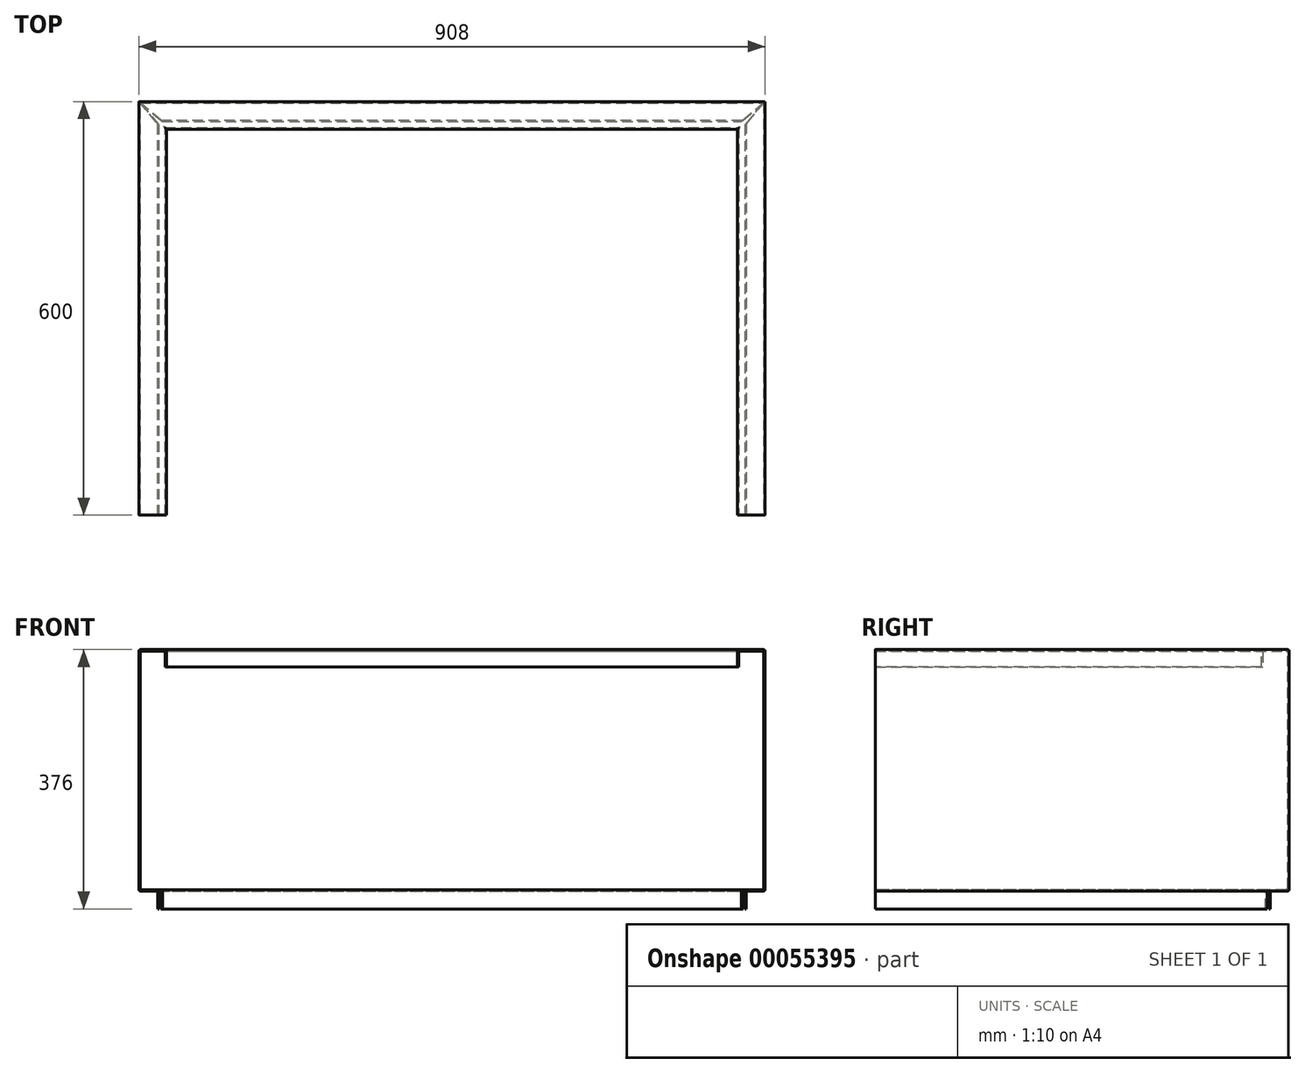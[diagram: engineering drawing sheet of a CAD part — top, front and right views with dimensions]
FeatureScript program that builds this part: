
annotation { "Feature Type Name" : "Feature", "Feature Type Description" : "" }
export const myFeature = defineFeature(function(context is Context, id is Id, definition is map)
    precondition{}
    {
        {
            var Q0;
            Q0=qCreatedBy(makeId("Front.planeOp"),FACE);
            var sketch = newSketch(context, id + "F0", { "sketchPlane" : qUnion([Q0])});
            skLineSegment(sketch, "E0", {"start": v(40, -25) * mm, "end": v(40, 0) * mm});
            skLineSegment(sketch, "E1", {"start": v(40, 0) * mm, "end": v(0, 0) * mm});
            skLineSegment(sketch, "E2", {"start": v(0, 0) * mm, "end": v(0, -350) * mm});
            skLineSegment(sketch, "E3", {"start": v(0, -350) * mm, "end": v(27, -350) * mm});
            skLineSegment(sketch, "E4", {"start": v(27, -350) * mm, "end": v(27, -376) * mm});
            skLineSegment(sketch, "E5.0", {"start": v(29, -348) * mm, "end": v(29, -376) * mm});
            skLineSegment(sketch, "E5.1", {"start": v(38, -25) * mm, "end": v(38, -2) * mm});
            skLineSegment(sketch, "E5.2", {"start": v(38, -2) * mm, "end": v(2, -2) * mm});
            skLineSegment(sketch, "E5.3", {"start": v(2, -2) * mm, "end": v(2, -348) * mm});
            skLineSegment(sketch, "E5.4", {"start": v(2, -348) * mm, "end": v(29, -348) * mm});
            skLineSegment(sketch, "E6", {"start": v(38, -25) * mm, "end": v(40, -25) * mm});
            skLineSegment(sketch, "E7", {"start": v(27, -376) * mm, "end": v(29, -376) * mm});
            skSolve(sketch);
        }
        {
            var Q0;
            Q0=qCreatedBy(makeId("Top.planeOp"),FACE);
            var sketch = newSketch(context, id + "F1", { "sketchPlane" : qUnion([Q0])});
            skLineSegment(sketch, "E8", {"start": v(0, 0) * mm, "end": v(0, 600) * mm});
            skLineSegment(sketch, "E9", {"start": v(0, 600) * mm, "end": v(908, 600) * mm});
            skLineSegment(sketch, "E10", {"start": v(908, 600) * mm, "end": v(908, 0) * mm});
            skSolve(sketch);
        }
        {
            var Q0;
            Q0=qSketchRegion(id+"F0",true);
            var Q1;
            Q1=qConstructionFilter(qBodyType(qCreatedBy(id+"F1",EDGE),BodyType.WIRE),ConstructionObject.NO);
            sweep(context, id + "F2", {"profiles" : qUnion([Q0]), "path" : qUnion([Q1])});
        }
        {
            var Q0;
            Q0=makeQuery(id+"F2.opSweep","SWEPT_FACE",FACE,{"disambiguationData":[OSD([sQuery(id+"F0.wireOp",EDGE,"E5.4"),sQuery(id+"F1.wireOp",EDGE,"E8")])]});
            var sketch = newSketch(context, id + "F3", { "sketchPlane" : qUnion([Q0])});
            skLineSegment(sketch, "E11", {"start": v(2, 598) * mm, "end": v(29, 565.82) * mm});
            skLineSegment(sketch, "E12", {"start": v(29, 565.82) * mm, "end": v(34.18, 571) * mm});
            skLineSegment(sketch, "E13", {"start": v(34.18, 571) * mm, "end": v(2, 598) * mm});
            skLineSegment(sketch, "E14", {"start": v(906, 598) * mm, "end": v(879, 565.82) * mm});
            skLineSegment(sketch, "E15", {"start": v(879, 565.82) * mm, "end": v(873.82, 571) * mm});
            skLineSegment(sketch, "E16", {"start": v(873.82, 571) * mm, "end": v(906, 598) * mm});
            skSolve(sketch);
        }
        {
            var Q0;
            {var subQ0=sQuery(id+"F3.wireOp",EDGE,"E14");Q0=makeQuery(id+"F3.imprint","IMPRINT",FACE,{"disambiguationData":[TD([[makeQuery(id+"F3.imprint","IMPRINT",EDGE,{"derivedFrom":subQ0}),-1.0]])]});}
            var Q1;
            {var subQ0=sQuery(id+"F3.wireOp",EDGE,"E11");Q1=makeQuery(id+"F3.imprint","IMPRINT",FACE,{"disambiguationData":[TD([[makeQuery(id+"F3.imprint","IMPRINT",EDGE,{"derivedFrom":subQ0}),1.0]])]});}
            extrude(context, id + "F4", {"entities" : qUnion([Q0, Q1]), "operationType" : NewBodyOperationType.REMOVE, "oppositeDirection" : true, "depth" : 30 * mm});
        }
        {
            var Q0;
            Q0=makeQuery(id+"F2.opSweep","SWEPT_EDGE",EDGE,{"disambiguationData":[OSD([sQuery(id+"F0.wireOp",EDGE,"E0"),sQuery(id+"F0.wireOp",EDGE,"E1"),sQuery(id+"F1.wireOp",EDGE,"E8")])]});
            var Q1;
            Q1=makeQuery(id+"F2.opSweep","SWEPT_EDGE",EDGE,{"disambiguationData":[OSD([sQuery(id+"F0.wireOp",EDGE,"E1"),sQuery(id+"F0.wireOp",EDGE,"E2"),sQuery(id+"F1.wireOp",EDGE,"E8")])]});
            var Q2;
            Q2=makeQuery(id+"F2.opSweep","SWEPT_EDGE",EDGE,{"disambiguationData":[OSD([sQuery(id+"F0.wireOp",EDGE,"E0"),sQuery(id+"F0.wireOp",EDGE,"E1"),sQuery(id+"F1.wireOp",EDGE,"E9")])]});
            var Q3;
            Q3=makeQuery(id+"F2.opSweep","SWEPT_EDGE",EDGE,{"disambiguationData":[OSD([sQuery(id+"F0.wireOp",EDGE,"E1"),sQuery(id+"F0.wireOp",EDGE,"E2"),sQuery(id+"F1.wireOp",EDGE,"E9")])]});
            var Q4;
            Q4=makeQuery(id+"F2.opSweep","SWEPT_EDGE",EDGE,{"disambiguationData":[OSD([sQuery(id+"F0.wireOp",EDGE,"E0"),sQuery(id+"F0.wireOp",EDGE,"E1"),sQuery(id+"F1.wireOp",EDGE,"E10")])]});
            var Q5;
            Q5=makeQuery(id+"F2.opSweep","SWEPT_EDGE",EDGE,{"disambiguationData":[OSD([sQuery(id+"F0.wireOp",EDGE,"E1"),sQuery(id+"F0.wireOp",EDGE,"E2"),sQuery(id+"F1.wireOp",EDGE,"E10")])]});
            var Q6;
            Q6=makeQuery(id+"F2.opSweep","MID_CAP_EDGE",EDGE,{"disambiguationData":[OSD([sQuery(id+"F0.wireOp",EDGE,"E2"),sQuery(id+"F1.wireOp",VERTEX,"E10.start")])],"capPos":2.0});
            var Q7;
            Q7=makeQuery(id+"F2.opSweep","SWEPT_EDGE",EDGE,{"disambiguationData":[OSD([sQuery(id+"F0.wireOp",EDGE,"E2"),sQuery(id+"F0.wireOp",EDGE,"E3"),sQuery(id+"F1.wireOp",EDGE,"E10")])]});
            var Q8;
            Q8=makeQuery(id+"F2.opSweep","SWEPT_EDGE",EDGE,{"disambiguationData":[OSD([sQuery(id+"F0.wireOp",EDGE,"E5.0"),sQuery(id+"F0.wireOp",EDGE,"E5.4"),sQuery(id+"F1.wireOp",EDGE,"E8")])]});
            var Q9;
            Q9=makeQuery(id+"F2.opSweep","SWEPT_EDGE",EDGE,{"disambiguationData":[OSD([sQuery(id+"F0.wireOp",EDGE,"E5.3"),sQuery(id+"F0.wireOp",EDGE,"E5.4"),sQuery(id+"F1.wireOp",EDGE,"E8")])]});
            var Q10;
            Q10=makeQuery(id+"F2.opSweep","SWEPT_EDGE",EDGE,{"disambiguationData":[OSD([sQuery(id+"F0.wireOp",EDGE,"E5.3"),sQuery(id+"F0.wireOp",EDGE,"E5.4"),sQuery(id+"F1.wireOp",EDGE,"E9")])]});
            var Q11;
            Q11=makeQuery(id+"F2.opSweep","SWEPT_EDGE",EDGE,{"disambiguationData":[OSD([sQuery(id+"F0.wireOp",EDGE,"E5.0"),sQuery(id+"F0.wireOp",EDGE,"E5.4"),sQuery(id+"F1.wireOp",EDGE,"E9")])]});
            var Q12;
            Q12=makeQuery(id+"F2.opSweep","SWEPT_EDGE",EDGE,{"disambiguationData":[OSD([sQuery(id+"F0.wireOp",EDGE,"E5.0"),sQuery(id+"F0.wireOp",EDGE,"E5.4"),sQuery(id+"F1.wireOp",EDGE,"E10")])]});
            var Q13;
            Q13=makeQuery(id+"F2.opSweep","SWEPT_EDGE",EDGE,{"disambiguationData":[OSD([sQuery(id+"F0.wireOp",EDGE,"E3"),sQuery(id+"F0.wireOp",EDGE,"E4"),sQuery(id+"F1.wireOp",EDGE,"E10")])]});
            var Q14;
            Q14=makeQuery(id+"F2.opSweep","SWEPT_EDGE",EDGE,{"disambiguationData":[OSD([sQuery(id+"F0.wireOp",EDGE,"E5.3"),sQuery(id+"F0.wireOp",EDGE,"E5.4"),sQuery(id+"F1.wireOp",EDGE,"E10")])]});
            var Q15;
            Q15=makeQuery(id+"F2.opSweep","SWEPT_EDGE",EDGE,{"disambiguationData":[OSD([sQuery(id+"F0.wireOp",EDGE,"E5.2"),sQuery(id+"F0.wireOp",EDGE,"E5.3"),sQuery(id+"F1.wireOp",EDGE,"E8")])]});
            var Q16;
            Q16=makeQuery(id+"F2.opSweep","SWEPT_EDGE",EDGE,{"disambiguationData":[OSD([sQuery(id+"F0.wireOp",EDGE,"E5.2"),sQuery(id+"F0.wireOp",EDGE,"E5.3"),sQuery(id+"F1.wireOp",EDGE,"E9")])]});
            var Q17;
            Q17=makeQuery(id+"F2.opSweep","SWEPT_EDGE",EDGE,{"disambiguationData":[OSD([sQuery(id+"F0.wireOp",EDGE,"E5.1"),sQuery(id+"F0.wireOp",EDGE,"E5.2"),sQuery(id+"F1.wireOp",EDGE,"E8")])]});
            var Q18;
            Q18=makeQuery(id+"F2.opSweep","SWEPT_EDGE",EDGE,{"disambiguationData":[OSD([sQuery(id+"F0.wireOp",EDGE,"E5.1"),sQuery(id+"F0.wireOp",EDGE,"E5.2"),sQuery(id+"F1.wireOp",EDGE,"E9")])]});
            var Q19;
            Q19=makeQuery(id+"F2.opSweep","SWEPT_EDGE",EDGE,{"disambiguationData":[OSD([sQuery(id+"F0.wireOp",EDGE,"E5.1"),sQuery(id+"F0.wireOp",EDGE,"E5.2"),sQuery(id+"F1.wireOp",EDGE,"E10")])]});
            var Q20;
            Q20=makeQuery(id+"F2.opSweep","SWEPT_EDGE",EDGE,{"disambiguationData":[OSD([sQuery(id+"F0.wireOp",EDGE,"E5.2"),sQuery(id+"F0.wireOp",EDGE,"E5.3"),sQuery(id+"F1.wireOp",EDGE,"E10")])]});
            var Q21;
            Q21=makeQuery(id+"F2.opSweep","SWEPT_EDGE",EDGE,{"disambiguationData":[OSD([sQuery(id+"F0.wireOp",EDGE,"E3"),sQuery(id+"F0.wireOp",EDGE,"E4"),sQuery(id+"F1.wireOp",EDGE,"E8")])]});
            var Q22;
            Q22=makeQuery(id+"F2.opSweep","SWEPT_EDGE",EDGE,{"disambiguationData":[OSD([sQuery(id+"F0.wireOp",EDGE,"E2"),sQuery(id+"F0.wireOp",EDGE,"E3"),sQuery(id+"F1.wireOp",EDGE,"E8")])]});
            var Q23;
            Q23=makeQuery(id+"F2.opSweep","SWEPT_EDGE",EDGE,{"disambiguationData":[OSD([sQuery(id+"F0.wireOp",EDGE,"E3"),sQuery(id+"F0.wireOp",EDGE,"E4"),sQuery(id+"F1.wireOp",EDGE,"E9")])]});
            var Q24;
            Q24=makeQuery(id+"F2.opSweep","SWEPT_EDGE",EDGE,{"disambiguationData":[OSD([sQuery(id+"F0.wireOp",EDGE,"E2"),sQuery(id+"F0.wireOp",EDGE,"E3"),sQuery(id+"F1.wireOp",EDGE,"E9")])]});
            fillet(context, id + "F5", {"entities" : qUnion([Q0, Q1, Q2, Q3, Q4, Q5, Q6, Q7, Q8, Q9, Q10, Q11, Q12, Q13, Q14, Q15, Q16, Q17, Q18, Q19, Q20, Q21, Q22, Q23, Q24]), "radius" : 2 * mm, "tangentPropagation" : true, "allowEdgeOverflow" : false});
        }
    });
